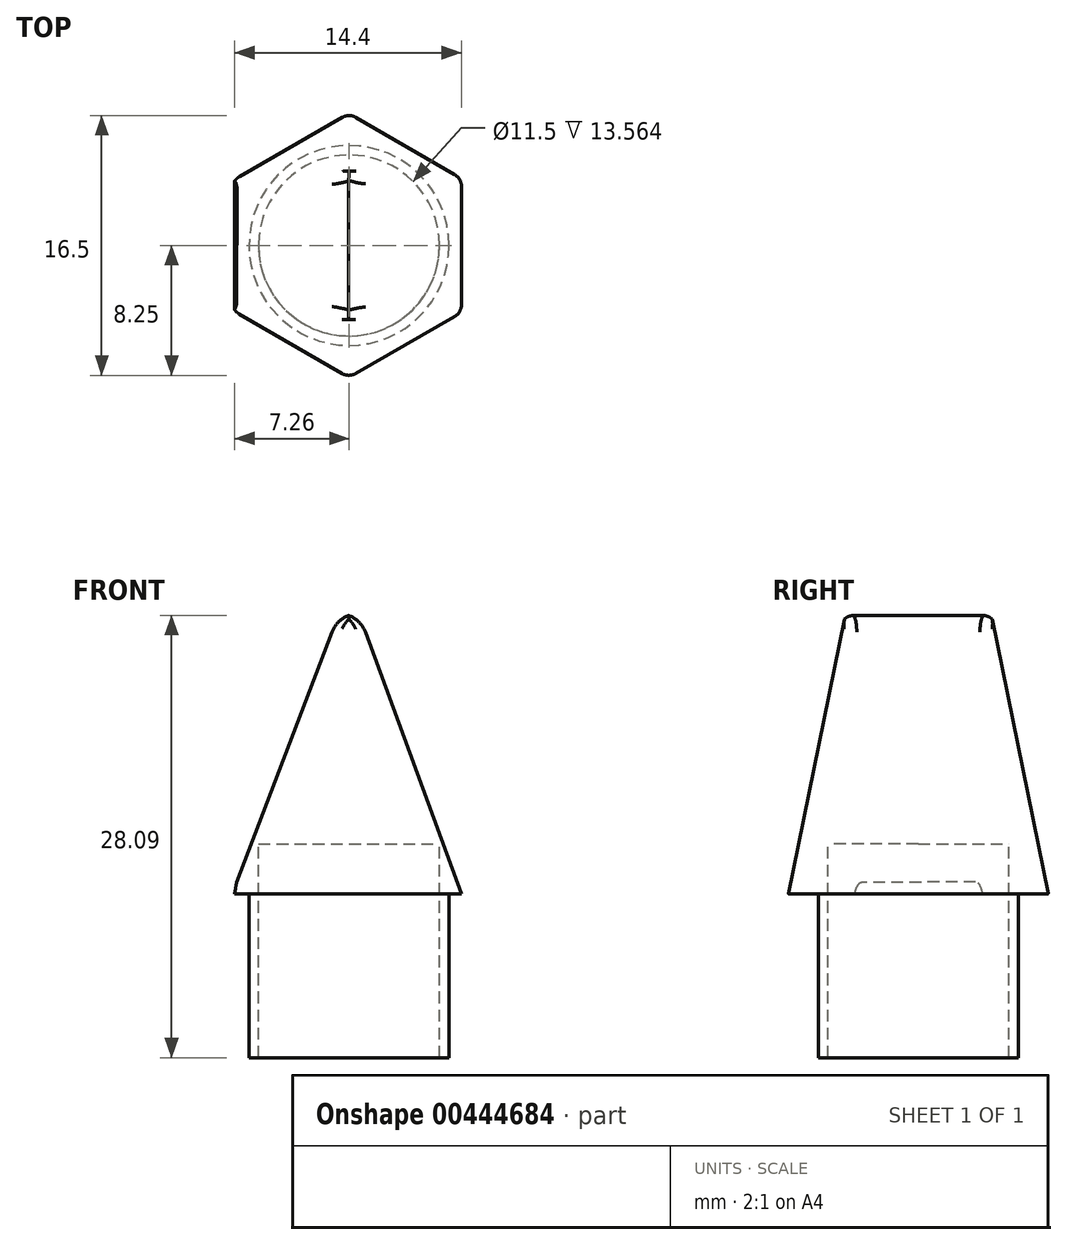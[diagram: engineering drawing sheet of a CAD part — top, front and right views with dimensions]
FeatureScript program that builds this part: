
annotation { "Feature Type Name" : "Feature", "Feature Type Description" : "" }
export const myFeature = defineFeature(function(context is Context, id is Id, definition is map)
    precondition{}
    {
        {
            var Q0;
            Q0=qCreatedBy(makeId("Top.planeOp"),FACE);
            var sketch = newSketch(context, id + "F0", { "sketchPlane" : qUnion([Q0])});
            skCircle(sketch, "E0", {"center": v(0, 0) * mm, "radius": 6.35 * mm});
            skSolve(sketch);
        }
        {
            var Q0;
            Q0 = qSketchRegion(id + "F0", true);
            extrude(context, id + "F1", {"entities" : qUnion([Q0]), "depth" : 11.43 * mm});
        }
        {
            var Q0;
            Q0=qCreatedBy(makeId("Top.planeOp"),FACE);
            cPlane(context, id + "F2", {"entities" : qUnion([Q0]), "cplaneType" : CPlaneType.OFFSET, "offset" : 10.4 * mm, "width" : 152.4 * mm, "height" : 152.4 * mm});
        }
        {
            var Q0;
            Q0=qCreatedBy(id+"F2.planeOp",FACE);
            var sketch = newSketch(context, id + "F3", { "sketchPlane" : qUnion([Q0])});
            skCircle(sketch, "E1.cCircle", {"center": v(0, 0) * mm, "radius": 7.86 * mm, "construction": true});
            skLineSegment(sketch, "E1.0", {"start": v(7.86, -4.55) * mm, "end": v(-0.01, -9.08) * mm});
            skLineSegment(sketch, "E1.1", {"start": v(-0.01, -9.08) * mm, "end": v(-7.87, -4.53) * mm});
            skLineSegment(sketch, "E1.2", {"start": v(-7.87, -4.53) * mm, "end": v(-7.86, 4.55) * mm});
            skLineSegment(sketch, "E1.3", {"start": v(-7.86, 4.55) * mm, "end": v(0.01, 9.08) * mm});
            skLineSegment(sketch, "E1.4", {"start": v(0.01, 9.08) * mm, "end": v(7.87, 4.53) * mm});
            skLineSegment(sketch, "E1.5", {"start": v(7.87, 4.53) * mm, "end": v(7.86, -4.55) * mm});
            skPoint(sketch, "E1.0.midPoint", {"position": v(3.92, -6.82) * mm});
            skSolve(sketch);
        }
        {
            var Q0;
            Q0 = qSketchRegion(id + "F3", true);
            extrude(context, id + "F4", {"entities" : qUnion([Q0]), "operationType" : NewBodyOperationType.ADD, "depth" : 17.78 * mm});
        }
        {
            var Q0;
            Q0=makeQuery(id+"F4.opExtrude","CAP_EDGE",EDGE,{"disambiguationData":[OSD([sQuery(id+"F3.wireOp",EDGE,"E1.0")])],"isStart":false});
            var Q1;
            Q1=makeQuery(id+"F4.opExtrude","CAP_EDGE",EDGE,{"disambiguationData":[OSD([sQuery(id+"F3.wireOp",EDGE,"E1.3")])],"isStart":false});
            var Q2;
            Q2=makeQuery(id+"F4.opExtrude","CAP_EDGE",EDGE,{"disambiguationData":[OSD([sQuery(id+"F3.wireOp",EDGE,"E1.5")])],"isStart":false});
            var Q3;
            Q3=makeQuery(id+"F4.opExtrude","CAP_EDGE",EDGE,{"disambiguationData":[OSD([sQuery(id+"F3.wireOp",EDGE,"E1.4")])],"isStart":false});
            var Q4;
            Q4=makeQuery(id+"F4.opExtrude","CAP_EDGE",EDGE,{"disambiguationData":[OSD([sQuery(id+"F3.wireOp",EDGE,"E1.2")])],"isStart":false});
            var Q5;
            Q5=makeQuery(id+"F4.opExtrude","CAP_FACE",FACE,{"disambiguationData":[OSD([sQuery(id+"F3.wireOp",EDGE,"E1.0"),sQuery(id+"F3.wireOp",EDGE,"E1.1"),sQuery(id+"F3.wireOp",EDGE,"E1.2"),sQuery(id+"F3.wireOp",EDGE,"E1.3"),sQuery(id+"F3.wireOp",EDGE,"E1.4"),sQuery(id+"F3.wireOp",EDGE,"E1.5")])],"isStart":false});
            chamfer(context, id + "F5", {"entities" : qUnion([Q0, Q1, Q2, Q3, Q4, Q5]), "chamferType" : ChamferType.OFFSET_ANGLE, "width" : 21.2 * mm, "oppositeDirection" : false, "angle" : 10 * degree, "tangentPropagation" : true});
        }
        {
            var Q0;
            Q0=qCreatedBy(makeId("Front.planeOp"),FACE);
            var sketch = newSketch(context, id + "F6", { "sketchPlane" : qUnion([Q0])});
            skLineSegment(sketch, "E2", {"start": v(0, 29.87) * mm, "end": v(-8.18, 8.38) * mm});
            skLineSegment(sketch, "E3", {"start": v(-8.18, 8.38) * mm, "end": v(-8.18, 29.87) * mm});
            skLineSegment(sketch, "E4", {"start": v(-8.18, 29.87) * mm, "end": v(7.64, 29.87) * mm});
            skLineSegment(sketch, "E5", {"start": v(7.64, 29.87) * mm, "end": v(7.64, 9.05) * mm});
            skLineSegment(sketch, "E6", {"start": v(7.64, 9.05) * mm, "end": v(0, 29.87) * mm});
            skSolve(sketch);
        }
        {
            var Q0;
            Q0 = qSketchRegion(id + "F6", true);
            extrude(context, id + "F7", {"entities" : qUnion([Q0]), "operationType" : NewBodyOperationType.REMOVE, "endBound" : BoundingType.SYMMETRIC, "oppositeDirection" : true, "depth" : 25.4 * mm});
        }
        {
            var Q0;
            Q0=makeQuery(id+"F7.boolean.opBoolean","INTERSECT",EDGE,{"derivedFrom":[makeQuery(id+"F4.opExtrude","CAP_FACE",FACE,{"disambiguationData":[OSD([sQuery(id+"F3.wireOp",EDGE,"E1.0"),sQuery(id+"F3.wireOp",EDGE,"E1.1"),sQuery(id+"F3.wireOp",EDGE,"E1.2"),sQuery(id+"F3.wireOp",EDGE,"E1.3"),sQuery(id+"F3.wireOp",EDGE,"E1.4"),sQuery(id+"F3.wireOp",EDGE,"E1.5")])],"isStart":false}),makeQuery(id+"F7.opExtrude","SWEPT_FACE",FACE,{"disambiguationData":[OSD([sQuery(id+"F6.wireOp",EDGE,"E6")])]})]});
            var Q1;
            Q1=makeQuery(id+"F7.boolean.opBoolean","INTERSECT",EDGE,{"derivedFrom":[makeQuery(id+"F4.opExtrude","CAP_FACE",FACE,{"disambiguationData":[OSD([sQuery(id+"F3.wireOp",EDGE,"E1.0"),sQuery(id+"F3.wireOp",EDGE,"E1.1"),sQuery(id+"F3.wireOp",EDGE,"E1.2"),sQuery(id+"F3.wireOp",EDGE,"E1.3"),sQuery(id+"F3.wireOp",EDGE,"E1.4"),sQuery(id+"F3.wireOp",EDGE,"E1.5")])],"isStart":false}),makeQuery(id+"F7.opExtrude","SWEPT_FACE",FACE,{"disambiguationData":[OSD([sQuery(id+"F6.wireOp",EDGE,"E2")])]})]});
            fillet(context, id + "F8", {"entities" : qUnion([Q0, Q1]), "radius" : 1.78 * mm, "tangentPropagation" : true, "allowEdgeOverflow" : false});
        }
        {
            var Q0;
            Q0=makeQuery(id+"F5.opChamfer","BLEND_EDGE",EDGE,{"blendedFrom":[makeQuery(id+"F4.opExtrude","CAP_EDGE",EDGE,{"disambiguationData":[OSD([sQuery(id+"F3.wireOp",EDGE,"E1.3")])],"isStart":false}),makeQuery(id+"F4.opExtrude","CAP_EDGE",EDGE,{"disambiguationData":[OSD([sQuery(id+"F3.wireOp",EDGE,"E1.4")])],"isStart":false})],"blendedInto":[]});
            var Q1;
            Q1=makeQuery(id+"F7.boolean.opBoolean","INTERSECT",EDGE,{"derivedFrom":[makeQuery(id+"F5.opChamfer","BLEND_FACE",FACE,{"disambiguationData":[OSD([sQuery(id+"F3.wireOp",EDGE,"E1.4")])]}),makeQuery(id+"F7.opExtrude","SWEPT_FACE",FACE,{"disambiguationData":[OSD([sQuery(id+"F6.wireOp",EDGE,"E6")])]})]});
            var Q2;
            Q2=makeQuery(id+"F7.boolean.opBoolean","INTERSECT",EDGE,{"derivedFrom":[makeQuery(id+"F5.opChamfer","BLEND_FACE",FACE,{"disambiguationData":[OSD([sQuery(id+"F3.wireOp",EDGE,"E1.0")])]}),makeQuery(id+"F7.opExtrude","SWEPT_FACE",FACE,{"disambiguationData":[OSD([sQuery(id+"F6.wireOp",EDGE,"E6")])]})]});
            var Q3;
            Q3=makeQuery(id+"F5.opChamfer","BLEND_EDGE",EDGE,{"blendedFrom":[makeQuery(id+"F4.opExtrude","CAP_EDGE",EDGE,{"disambiguationData":[OSD([sQuery(id+"F3.wireOp",EDGE,"E1.0")])],"isStart":false}),makeQuery(id+"F4.opExtrude","CAP_EDGE",EDGE,{"disambiguationData":[OSD([sQuery(id+"F3.wireOp",EDGE,"E1.1")])],"isStart":false})],"blendedInto":[]});
            var Q4;
            Q4=makeQuery(id+"F7.boolean.opBoolean","INTERSECT",EDGE,{"derivedFrom":[makeQuery(id+"F5.opChamfer","BLEND_FACE",FACE,{"disambiguationData":[OSD([sQuery(id+"F3.wireOp",EDGE,"E1.1")])]}),makeQuery(id+"F7.opExtrude","SWEPT_FACE",FACE,{"disambiguationData":[OSD([sQuery(id+"F6.wireOp",EDGE,"E2")])]})]});
            var Q5;
            Q5=makeQuery(id+"F7.boolean.opBoolean","INTERSECT",EDGE,{"derivedFrom":[makeQuery(id+"F5.opChamfer","BLEND_FACE",FACE,{"disambiguationData":[OSD([sQuery(id+"F3.wireOp",EDGE,"E1.3")])]}),makeQuery(id+"F7.opExtrude","SWEPT_FACE",FACE,{"disambiguationData":[OSD([sQuery(id+"F6.wireOp",EDGE,"E2")])]})]});
            fillet(context, id + "F9", {"entities" : qUnion([Q0, Q1, Q2, Q3, Q4, Q5]), "radius" : 0.87 * mm, "tangentPropagation" : true, "allowEdgeOverflow" : false});
        }
        {
            var Q0;
            Q0=makeQuery(id+"F1.opExtrude","CAP_FACE",FACE,{"disambiguationData":[OSD([sQuery(id+"F0.wireOp",EDGE,"E0")])],"isStart":true});
            var sketch = newSketch(context, id + "F10", { "sketchPlane" : qUnion([Q0])});
            skCircle(sketch, "E7", {"center": v(0, 0) * mm, "radius": 5.75 * mm});
            skSolve(sketch);
        }
        {
            var Q0;
            Q0=makeQuery(id+"F10.imprint","IMPRINT",FACE,{"disambiguationData":[TD([[makeQuery(id+"F10.imprint","IMPRINT",EDGE,{"derivedFrom":sQuery(id+"F10.wireOp",EDGE,"E7")}),1.0]])]});
            var Q1;
            Q1=sQuery(id+"F10.wireOp",EDGE,"E7");
            extrude(context, id + "F11", {"entities" : qUnion([Q0]), "operationType" : NewBodyOperationType.REMOVE, "surfaceEntities" : qUnion([Q1]), "endBound" : BoundingType.SYMMETRIC, "depth" : 27.13 * mm});
        }
    });
